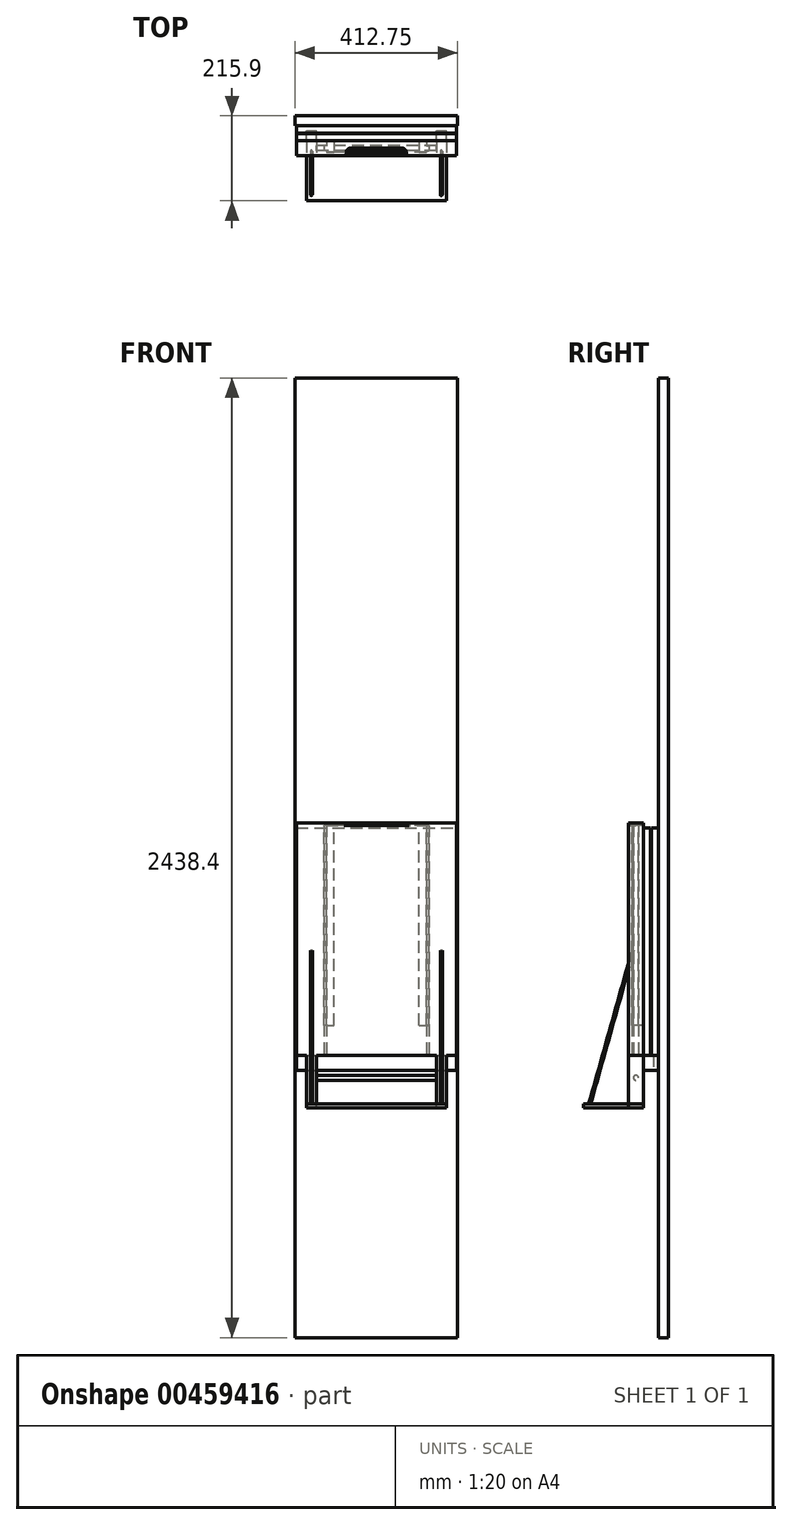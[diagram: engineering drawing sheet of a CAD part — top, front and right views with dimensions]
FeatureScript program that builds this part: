
annotation { "Feature Type Name" : "Feature", "Feature Type Description" : "" }
export const myFeature = defineFeature(function(context is Context, id is Id, definition is map)
    precondition{}
    {
        {
            var Q0;
            Q0=qCreatedBy(makeId("Front.planeOp"),FACE);
            var sketch = newSketch(context, id + "F0", { "sketchPlane" : qUnion([Q0])});
            skLineSegment(sketch, "E0.bottom", {"start": v(0, 0) * mm, "end": v(412.75, 0) * mm});
            skLineSegment(sketch, "E0.top", {"start": v(0, 2438.4) * mm, "end": v(412.75, 2438.4) * mm});
            skLineSegment(sketch, "E0.left", {"start": v(0, 0) * mm, "end": v(0, 2438.4) * mm});
            skLineSegment(sketch, "E0.right", {"start": v(412.75, 0) * mm, "end": v(412.75, 2438.4) * mm});
            skSolve(sketch);
        }
        {
            var Q0;
            Q0=qSketchRegion(id+"F0",true);
            extrude(context, id + "F1", {"entities" : qUnion([Q0]), "depth" : 25.4 * mm});
        }
        {
            var Q0;
            Q0=makeQuery(id+"F1.opExtrude","CAP_FACE",FACE,{"disambiguationData":[OSD([sQuery(id+"F0.wireOp",EDGE,"E0.bottom"),sQuery(id+"F0.wireOp",EDGE,"E0.top"),sQuery(id+"F0.wireOp",EDGE,"E0.left"),sQuery(id+"F0.wireOp",EDGE,"E0.right")])],"isStart":false});
            var sketch = newSketch(context, id + "F2", { "sketchPlane" : qUnion([Q0])});
            skLineSegment(sketch, "E1", {"start": v(206.38, 0) * mm, "end": v(206.38, 1295.4) * mm, "construction": true});
            skPoint(sketch, "E2", {"position": v(206.38, 736.6) * mm});
            skSolve(sketch);
        }
        {
            var Q0;
            Q0=makeQuery(id+"F2.imprint","IMPRINT",FACE,{"disambiguationData":[TD([[makeQuery(id+"F2.imprint","IMPRINT",EDGE,{"derivedFrom":makeQuery(id+"F1.opExtrude","CAP_EDGE",EDGE,{"disambiguationData":[OSD([sQuery(id+"F0.wireOp",EDGE,"E0.bottom")])],"isStart":false})}),1.0]])]});
            var sketch = newSketch(context, id + "F3", { "sketchPlane" : qUnion([Q0])});
            skLineSegment(sketch, "E3.bottom", {"start": v(3.17, 717.55) * mm, "end": v(409.58, 717.55) * mm});
            skLineSegment(sketch, "E3.top", {"start": v(3.18, 679.45) * mm, "end": v(409.57, 679.45) * mm});
            skLineSegment(sketch, "E3.left", {"start": v(3.17, 717.55) * mm, "end": v(3.17, 679.45) * mm});
            skLineSegment(sketch, "E3.right", {"start": v(409.57, 717.55) * mm, "end": v(409.57, 679.45) * mm});
            skLineSegment(sketch, "E4", {"start": v(206.37, 717.55) * mm, "end": v(206.37, 764.95) * mm, "construction": true});
            skSolve(sketch);
        }
        {
            var Q0;
            Q0=qSketchRegion(id+"F3",true);
            extrude(context, id + "F4", {"entities" : qUnion([Q0]), "depth" : 38.1 * mm});
        }
        {
            var Q0;
            Q0=makeQuery(id+"F4.opExtrude","SWEPT_FACE",FACE,{"disambiguationData":[OSD([sQuery(id+"F3.wireOp",EDGE,"E3.bottom")])]});
            var sketch = newSketch(context, id + "F5", { "sketchPlane" : qUnion([Q0])});
            skLineSegment(sketch, "E5.bottom", {"start": v(3.17, -25.4) * mm, "end": v(409.58, -25.4) * mm});
            skLineSegment(sketch, "E5.top", {"start": v(3.17, -43.66) * mm, "end": v(409.58, -43.66) * mm});
            skLineSegment(sketch, "E5.left", {"start": v(3.17, -25.4) * mm, "end": v(3.17, -43.66) * mm});
            skLineSegment(sketch, "E5.right", {"start": v(409.58, -25.4) * mm, "end": v(409.58, -43.66) * mm});
            skLineSegment(sketch, "E6.bottom", {"start": v(3.17, -63.5) * mm, "end": v(409.58, -63.5) * mm});
            skLineSegment(sketch, "E6.top", {"start": v(3.17, -45.24) * mm, "end": v(409.58, -45.24) * mm});
            skLineSegment(sketch, "E6.left", {"start": v(3.17, -63.5) * mm, "end": v(3.17, -45.24) * mm});
            skLineSegment(sketch, "E6.right", {"start": v(409.58, -63.5) * mm, "end": v(409.58, -45.24) * mm});
            skSolve(sketch);
        }
        {
            var Q0;
            Q0=qSketchRegion(id+"F5",true);
            var Q1;
            Q1=sQuery(id+"F2.wireOp",VERTEX,"E1.end");
            extrude(context, id + "F6", {"entities" : qUnion([Q0]), "endBound" : BoundingType.UP_TO_VERTEX, "endBoundEntityVertex" : qUnion([Q1]), "depth" : 25.4 * mm});
        }
        {
            var Q0;
            Q0=makeQuery(id+"F4.opExtrude","CAP_FACE",FACE,{"disambiguationData":[OSD([sQuery(id+"F3.wireOp",EDGE,"E3.bottom"),sQuery(id+"F3.wireOp",EDGE,"E3.top"),sQuery(id+"F3.wireOp",EDGE,"E3.left"),sQuery(id+"F3.wireOp",EDGE,"E3.right")])],"isStart":false});
            var sketch = newSketch(context, id + "F7", { "sketchPlane" : qUnion([Q0])});
            skLineSegment(sketch, "E7.bottom", {"start": v(3.17, 717.55) * mm, "end": v(28.57, 717.55) * mm});
            skLineSegment(sketch, "E7.top", {"start": v(3.17, 679.45) * mm, "end": v(28.57, 679.45) * mm});
            skLineSegment(sketch, "E7.left", {"start": v(3.17, 717.55) * mm, "end": v(3.17, 679.45) * mm});
            skLineSegment(sketch, "E7.right", {"start": v(28.57, 717.55) * mm, "end": v(28.57, 679.45) * mm});
            skLineSegment(sketch, "E8.bottom", {"start": v(409.57, 679.45) * mm, "end": v(384.17, 679.45) * mm});
            skLineSegment(sketch, "E8.top", {"start": v(409.57, 717.55) * mm, "end": v(384.17, 717.55) * mm});
            skLineSegment(sketch, "E8.left", {"start": v(409.57, 679.45) * mm, "end": v(409.57, 717.55) * mm});
            skLineSegment(sketch, "E8.right", {"start": v(384.17, 679.45) * mm, "end": v(384.17, 717.55) * mm});
            skSolve(sketch);
        }
        {
            var Q0;
            Q0=qSketchRegion(id+"F7",true);
            extrude(context, id + "F8", {"entities" : qUnion([Q0]), "depth" : 584.2 * mm});
        }
        {
            var Q0;
            Q0=makeQuery(id+"F8.opExtrude","CAP_FACE",FACE,{"disambiguationData":[OSD([sQuery(id+"F7.wireOp",EDGE,"E8.bottom"),sQuery(id+"F7.wireOp",EDGE,"E8.top"),sQuery(id+"F7.wireOp",EDGE,"E8.left"),sQuery(id+"F7.wireOp",EDGE,"E8.right")])],"isStart":false});
            var sketch = newSketch(context, id + "F9", { "sketchPlane" : qUnion([Q0])});
            skLineSegment(sketch, "E9.bottom", {"start": v(53.97, 717.55) * mm, "end": v(79.37, 717.55) * mm});
            skLineSegment(sketch, "E9.top", {"start": v(53.97, 679.45) * mm, "end": v(79.37, 679.45) * mm});
            skLineSegment(sketch, "E9.left", {"start": v(53.97, 717.55) * mm, "end": v(53.97, 679.45) * mm});
            skLineSegment(sketch, "E9.right", {"start": v(79.37, 717.55) * mm, "end": v(79.37, 704.85) * mm});
            skLineSegment(sketch, "E10.bottom", {"start": v(333.38, 717.55) * mm, "end": v(358.78, 717.55) * mm});
            skLineSegment(sketch, "E10.top", {"start": v(333.38, 679.45) * mm, "end": v(358.78, 679.45) * mm});
            skLineSegment(sketch, "E10.left", {"start": v(333.38, 717.55) * mm, "end": v(333.38, 704.85) * mm});
            skLineSegment(sketch, "E10.right", {"start": v(358.78, 717.55) * mm, "end": v(358.78, 679.45) * mm});
            skLineSegment(sketch, "E11", {"start": v(53.97, 698.5) * mm, "end": v(358.78, 698.5) * mm, "construction": true});
            skLineSegment(sketch, "E12", {"start": v(358.78, 698.5) * mm, "end": v(206.37, 698.5) * mm, "construction": true});
            skLineSegment(sketch, "E13", {"start": v(206.37, 698.5) * mm, "end": v(206.37, 1295.4) * mm, "construction": true});
            skLineSegment(sketch, "E14.bottom", {"start": v(79.37, 704.85) * mm, "end": v(73.02, 704.85) * mm});
            skLineSegment(sketch, "E14.top", {"start": v(79.37, 692.15) * mm, "end": v(73.02, 692.15) * mm});
            skLineSegment(sketch, "E14.right", {"start": v(73.02, 704.85) * mm, "end": v(73.02, 692.15) * mm});
            skLineSegment(sketch, "E15.bottom", {"start": v(333.38, 704.85) * mm, "end": v(339.73, 704.85) * mm});
            skLineSegment(sketch, "E15.top", {"start": v(333.38, 692.15) * mm, "end": v(339.73, 692.15) * mm});
            skLineSegment(sketch, "E15.right", {"start": v(339.73, 704.85) * mm, "end": v(339.73, 692.15) * mm});
            skLineSegment(sketch, "E16", {"start": v(73.02, 698.5) * mm, "end": v(91.35, 698.5) * mm, "construction": true});
            skLineSegment(sketch, "E17.trimOffspring", {"start": v(79.37, 692.15) * mm, "end": v(79.37, 679.45) * mm});
            skLineSegment(sketch, "E18.trimOffspring", {"start": v(333.38, 692.15) * mm, "end": v(333.38, 679.45) * mm});
            skSolve(sketch);
        }
        {
            var Q0;
            Q0=qSketchRegion(id+"F9",true);
            extrude(context, id + "F10", {"entities" : qUnion([Q0]), "depth" : 330.2 * mm, "hasSecondDirection" : true, "secondDirectionOppositeDirection" : true, "secondDirectionDepth" : 254 * mm});
        }
        {
            var Q0;
            Q0=makeQuery(id+"F10.opExtrude","CAP_FACE",FACE,{"disambiguationData":[OSD([sQuery(id+"F9.wireOp",EDGE,"E9.bottom"),sQuery(id+"F9.wireOp",EDGE,"E9.top"),sQuery(id+"F9.wireOp",EDGE,"E9.left"),sQuery(id+"F9.wireOp",EDGE,"E9.right"),sQuery(id+"F9.wireOp",EDGE,"E14.bottom"),sQuery(id+"F9.wireOp",EDGE,"E14.top"),sQuery(id+"F9.wireOp",EDGE,"E14.right"),sQuery(id+"F9.wireOp",EDGE,"E17.trimOffspring")])],"isStart":false});
            var sketch = newSketch(context, id + "F11", { "sketchPlane" : qUnion([Q0])});
            skLineSegment(sketch, "E19.bottom", {"start": v(53.97, 679.45) * mm, "end": v(358.78, 679.45) * mm});
            skLineSegment(sketch, "E19.top", {"start": v(53.97, 717.55) * mm, "end": v(358.78, 717.55) * mm});
            skLineSegment(sketch, "E19.left", {"start": v(53.97, 679.45) * mm, "end": v(53.97, 717.55) * mm});
            skLineSegment(sketch, "E19.right", {"start": v(358.78, 679.45) * mm, "end": v(358.78, 717.55) * mm});
            skSolve(sketch);
        }
        {
            var Q0;
            Q0=qSketchRegion(id+"F11",true);
            extrude(context, id + "F12", {"entities" : qUnion([Q0]), "depth" : 6.35 * mm});
        }
        {
            var Q0;
            Q0=makeQuery(id+"F8.opExtrude","CAP_FACE",FACE,{"disambiguationData":[OSD([sQuery(id+"F7.wireOp",EDGE,"E7.bottom"),sQuery(id+"F7.wireOp",EDGE,"E7.top"),sQuery(id+"F7.wireOp",EDGE,"E7.left"),sQuery(id+"F7.wireOp",EDGE,"E7.right")])],"isStart":false});
            var sketch = newSketch(context, id + "F13", { "sketchPlane" : qUnion([Q0])});
            skLineSegment(sketch, "E20.0", {"start": v(79.37, 717.55) * mm, "end": v(79.37, 704.85) * mm});
            skLineSegment(sketch, "E20.1", {"start": v(79.37, 704.85) * mm, "end": v(73.02, 704.85) * mm});
            skLineSegment(sketch, "E20.2", {"start": v(73.02, 704.85) * mm, "end": v(73.02, 692.15) * mm});
            skLineSegment(sketch, "E20.3", {"start": v(79.37, 692.15) * mm, "end": v(73.02, 692.15) * mm});
            skLineSegment(sketch, "E20.4", {"start": v(79.37, 692.15) * mm, "end": v(79.37, 679.45) * mm});
            skLineSegment(sketch, "E20.5", {"start": v(333.38, 717.55) * mm, "end": v(333.38, 704.85) * mm});
            skLineSegment(sketch, "E20.6", {"start": v(333.38, 704.85) * mm, "end": v(339.73, 704.85) * mm});
            skLineSegment(sketch, "E20.7", {"start": v(339.73, 704.85) * mm, "end": v(339.73, 692.15) * mm});
            skLineSegment(sketch, "E20.8", {"start": v(333.38, 692.15) * mm, "end": v(339.73, 692.15) * mm});
            skLineSegment(sketch, "E20.9", {"start": v(333.38, 692.15) * mm, "end": v(333.38, 679.45) * mm});
            skLineSegment(sketch, "E21", {"start": v(333.38, 717.55) * mm, "end": v(314.33, 717.55) * mm});
            skLineSegment(sketch, "E22", {"start": v(314.33, 717.55) * mm, "end": v(314.33, 679.45) * mm});
            skLineSegment(sketch, "E23", {"start": v(314.33, 679.45) * mm, "end": v(333.38, 679.45) * mm});
            skLineSegment(sketch, "E24", {"start": v(79.37, 717.55) * mm, "end": v(98.42, 717.55) * mm});
            skLineSegment(sketch, "E25", {"start": v(98.42, 717.55) * mm, "end": v(98.42, 679.45) * mm});
            skLineSegment(sketch, "E26", {"start": v(98.42, 679.45) * mm, "end": v(79.37, 679.45) * mm});
            skSolve(sketch);
        }
        {
            var Q0;
            Q0=qSketchRegion(id+"F13",true);
            extrude(context, id + "F14", {"entities" : qUnion([Q0]), "oppositeDirection" : true, "depth" : 508 * mm});
        }
        {
            var Q0;
            Q0=makeQuery(id+"F14.opExtrude","SWEPT_FACE",FACE,{"disambiguationData":[OSD([sQuery(id+"F13.wireOp",EDGE,"E23")])]});
            var sketch = newSketch(context, id + "F15", { "sketchPlane" : qUnion([Q0])});
            skLineSegment(sketch, "E27.bottom", {"start": v(44.15, 977.9) * mm, "end": v(373.47, 977.9) * mm});
            skLineSegment(sketch, "E27.top", {"start": v(44.15, 63.5) * mm, "end": v(373.47, 63.5) * mm});
            skLineSegment(sketch, "E27.left", {"start": v(44.15, 977.9) * mm, "end": v(44.15, 63.5) * mm});
            skLineSegment(sketch, "E27.right", {"start": v(373.47, 977.9) * mm, "end": v(373.47, 63.5) * mm});
            skSolve(sketch);
        }
        {
            var Q0;
            Q0=qSketchRegion(id+"F15",true);
            extrude(context, id + "F16", {"entities" : qUnion([Q0]), "operationType" : NewBodyOperationType.REMOVE, "oppositeDirection" : true, "depth" : 9.52 * mm});
        }
        {
            var Q0;
            Q0=makeQuery(id+"F8.opExtrude","SWEPT_FACE",FACE,{"disambiguationData":[OSD([sQuery(id+"F7.wireOp",EDGE,"E8.bottom")])]});
            var sketch = newSketch(context, id + "F17", { "sketchPlane" : qUnion([Q0])});
            skLineSegment(sketch, "E28.bottom", {"start": v(53.97, 647.7) * mm, "end": v(358.78, 647.7) * mm});
            skLineSegment(sketch, "E28.top", {"start": v(53.97, 63.5) * mm, "end": v(358.78, 63.5) * mm});
            skLineSegment(sketch, "E28.left", {"start": v(53.97, 647.7) * mm, "end": v(53.97, 63.5) * mm});
            skLineSegment(sketch, "E28.right", {"start": v(358.78, 647.7) * mm, "end": v(358.78, 63.5) * mm});
            skSolve(sketch);
        }
        {
            var Q0;
            Q0=qSketchRegion(id+"F17",true);
            var Q1;
            {var subQ5=sQuery(id+"F9.wireOp",EDGE,"E9.left");Q1=makeQuery(id+"F16.boolean.opBoolean","COPY",FACE,{"disambiguationData":[TD([makeQuery(id+"F10.opExtrude","SWEPT_FACE",FACE,{"disambiguationData":[OSD([subQ5])]})])],"derivedFrom":makeQuery(id+"F16.opExtrude","CAP_FACE",FACE,{"disambiguationData":[OSD([sQuery(id+"F15.wireOp",EDGE,"E27.bottom"),sQuery(id+"F15.wireOp",EDGE,"E27.top"),sQuery(id+"F15.wireOp",EDGE,"E27.left"),sQuery(id+"F15.wireOp",EDGE,"E27.right")])],"isStart":false})});}
            extrude(context, id + "F18", {"entities" : qUnion([Q0]), "endBound" : BoundingType.UP_TO_SURFACE, "oppositeDirection" : true, "endBoundEntityFace" : qUnion([Q1]), "depth" : 25.4 * mm});
        }
        {
            var Q0;
            Q0=makeQuery(id+"F12.opExtrude","CAP_FACE",FACE,{"disambiguationData":[OSD([sQuery(id+"F11.wireOp",EDGE,"E19.bottom"),sQuery(id+"F11.wireOp",EDGE,"E19.top"),sQuery(id+"F11.wireOp",EDGE,"E19.left"),sQuery(id+"F11.wireOp",EDGE,"E19.right")])],"isStart":false});
            var sketch = newSketch(context, id + "F19", { "sketchPlane" : qUnion([Q0])});
            skLineSegment(sketch, "E29.top", {"start": v(139.7, 698.5) * mm, "end": v(273.05, 698.5) * mm});
            skLineSegment(sketch, "E29.left", {"start": v(130.17, 685.8) * mm, "end": v(130.17, 688.98) * mm});
            skLineSegment(sketch, "E29.right", {"start": v(282.57, 685.8) * mm, "end": v(282.57, 688.98) * mm});
            skLineSegment(sketch, "E30", {"start": v(206.37, 698.5) * mm, "end": v(206.37, 717.55) * mm, "construction": true});
            skPoint(sketch, "E31.visualSharp", {"position": v(130.17, 698.5) * mm});
            skArc(sketch, "E31.filletArc", {"start": v(139.7, 698.5) * mm, "mid": v(132.96, 695.71) * mm, "end": v(130.17, 688.98) * mm});
            skPoint(sketch, "E32.visualSharp", {"position": v(282.58, 698.5) * mm});
            skArc(sketch, "E32.filletArc", {"start": v(282.57, 688.98) * mm, "mid": v(279.79, 695.71) * mm, "end": v(273.05, 698.5) * mm});
            skLineSegment(sketch, "E33", {"start": v(123.82, 679.45) * mm, "end": v(104.54, 679.45) * mm});
            skLineSegment(sketch, "E34", {"start": v(104.54, 679.45) * mm, "end": v(95.15, 663.43) * mm});
            skLineSegment(sketch, "E35", {"start": v(95.15, 663.43) * mm, "end": v(306.09, 663.43) * mm});
            skLineSegment(sketch, "E36", {"start": v(306.09, 663.43) * mm, "end": v(306.09, 679.45) * mm});
            skLineSegment(sketch, "E37", {"start": v(306.09, 679.45) * mm, "end": v(288.92, 679.45) * mm});
            skPoint(sketch, "E38.visualSharp", {"position": v(130.17, 679.45) * mm});
            skArc(sketch, "E38.filletArc", {"start": v(123.82, 679.45) * mm, "mid": v(128.32, 681.3) * mm, "end": v(130.17, 685.8) * mm});
            skPoint(sketch, "E39.visualSharp", {"position": v(282.57, 679.45) * mm});
            skArc(sketch, "E39.filletArc", {"start": v(282.58, 685.8) * mm, "mid": v(284.43, 681.3) * mm, "end": v(288.92, 679.45) * mm});
            skSolve(sketch);
        }
        {
            var Q0;
            Q0=qSketchRegion(id+"F19",true);
            extrude(context, id + "F20", {"entities" : qUnion([Q0]), "operationType" : NewBodyOperationType.REMOVE, "oppositeDirection" : true, "depth" : 25.4 * mm});
        }
        {
            var Q0;
            Q0=makeQuery(id+"F8.opExtrude","SWEPT_FACE",FACE,{"disambiguationData":[OSD([sQuery(id+"F7.wireOp",EDGE,"E7.bottom")])]});
            var sketch = newSketch(context, id + "F21", { "sketchPlane" : qUnion([Q0])});
            skLineSegment(sketch, "E40.bottom", {"start": v(3.17, -63.5) * mm, "end": v(409.58, -63.5) * mm});
            skLineSegment(sketch, "E40.top", {"start": v(3.17, -647.7) * mm, "end": v(409.58, -647.7) * mm});
            skLineSegment(sketch, "E40.left", {"start": v(3.17, -63.5) * mm, "end": v(3.17, -647.7) * mm});
            skLineSegment(sketch, "E40.right", {"start": v(409.58, -63.5) * mm, "end": v(409.58, -647.7) * mm});
            skLineSegment(sketch, "E41.bottom", {"start": v(3.17, -650.88) * mm, "end": v(409.58, -650.88) * mm});
            skLineSegment(sketch, "E41.top", {"start": v(3.17, -1235.08) * mm, "end": v(409.58, -1235.08) * mm});
            skLineSegment(sketch, "E41.left", {"start": v(3.17, -650.88) * mm, "end": v(3.17, -1235.08) * mm});
            skLineSegment(sketch, "E41.right", {"start": v(409.58, -650.88) * mm, "end": v(409.58, -1235.08) * mm});
            skSolve(sketch);
        }
        {
            var Q0;
            Q0=qSketchRegion(id+"F21",true);
            extrude(context, id + "F22", {"entities" : qUnion([Q0]), "depth" : 19.05 * mm});
        }
        {
            var Q0;
            Q0=makeQuery(id+"F22.opExtrude","CAP_FACE",FACE,{"disambiguationData":[OSD([sQuery(id+"F21.wireOp",EDGE,"E40.bottom"),sQuery(id+"F21.wireOp",EDGE,"E40.top"),sQuery(id+"F21.wireOp",EDGE,"E40.left"),sQuery(id+"F21.wireOp",EDGE,"E40.right")])],"isStart":true});
            var sketch = newSketch(context, id + "F23", { "sketchPlane" : qUnion([Q0])});
            skLineSegment(sketch, "E42.bottom", {"start": v(28.57, 635) * mm, "end": v(53.97, 635) * mm});
            skLineSegment(sketch, "E42.top", {"start": v(28.57, 596.9) * mm, "end": v(53.97, 596.9) * mm});
            skLineSegment(sketch, "E42.left", {"start": v(28.57, 635) * mm, "end": v(28.57, 596.9) * mm});
            skLineSegment(sketch, "E42.right", {"start": v(53.97, 635) * mm, "end": v(53.97, 596.9) * mm});
            skLineSegment(sketch, "E43.bottom", {"start": v(358.78, 635) * mm, "end": v(384.17, 635) * mm});
            skLineSegment(sketch, "E43.top", {"start": v(358.78, 596.9) * mm, "end": v(384.17, 596.9) * mm});
            skLineSegment(sketch, "E43.left", {"start": v(358.78, 635) * mm, "end": v(358.78, 596.9) * mm});
            skLineSegment(sketch, "E43.right", {"start": v(384.17, 635) * mm, "end": v(384.17, 596.9) * mm});
            skSolve(sketch);
        }
        {
            var Q0;
            Q0=qSketchRegion(id+"F23",true);
            var Q1;
            Q1=makeQuery(id+"F1.opExtrude","SWEPT_FACE",FACE,{"disambiguationData":[OSD([sQuery(id+"F0.wireOp",EDGE,"E0.bottom")])]});
            extrude(context, id + "F24", {"entities" : qUnion([Q0]), "endBound" : BoundingType.UP_TO_SURFACE, "endBoundEntityFace" : qUnion([Q1]), "depth" : 25.4 * mm});
        }
        {
            var Q0;
            Q0=makeQuery(id+"F24.opExtrude","CAP_FACE",FACE,{"disambiguationData":[OSD([sQuery(id+"F23.wireOp",EDGE,"E43.bottom"),sQuery(id+"F23.wireOp",EDGE,"E43.top"),sQuery(id+"F23.wireOp",EDGE,"E43.left"),sQuery(id+"F23.wireOp",EDGE,"E43.right")])],"isStart":false});
            var sketch = newSketch(context, id + "F25", { "sketchPlane" : qUnion([Q0])});
            skLineSegment(sketch, "E44.bottom", {"start": v(28.57, 596.9) * mm, "end": v(384.17, 596.9) * mm});
            skLineSegment(sketch, "E44.top", {"start": v(28.57, 749.3) * mm, "end": v(384.17, 749.3) * mm});
            skLineSegment(sketch, "E44.left", {"start": v(28.57, 596.9) * mm, "end": v(28.57, 749.3) * mm});
            skLineSegment(sketch, "E44.right", {"start": v(384.17, 596.9) * mm, "end": v(384.17, 749.3) * mm});
            skSolve(sketch);
        }
        {
            var Q0;
            Q0=qSketchRegion(id+"F25",true);
            extrude(context, id + "F26", {"entities" : qUnion([Q0]), "oppositeDirection" : true, "depth" : 9.52 * mm});
        }
        {
            var Q0;
            Q0=makeQuery(id+"F4.opExtrude","SWEPT_FACE",FACE,{"disambiguationData":[OSD([sQuery(id+"F3.wireOp",EDGE,"E3.top")])]});
            var sketch = newSketch(context, id + "F27", { "sketchPlane" : qUnion([Q0])});
            skLineSegment(sketch, "E45.bottom", {"start": v(28.57, 63.5) * mm, "end": v(53.97, 63.5) * mm});
            skLineSegment(sketch, "E45.top", {"start": v(28.57, 38.1) * mm, "end": v(53.97, 38.1) * mm});
            skLineSegment(sketch, "E45.left", {"start": v(28.57, 63.5) * mm, "end": v(28.57, 38.1) * mm});
            skLineSegment(sketch, "E45.right", {"start": v(53.97, 63.5) * mm, "end": v(53.97, 38.1) * mm});
            skLineSegment(sketch, "E46.bottom", {"start": v(358.78, 63.5) * mm, "end": v(384.18, 63.5) * mm});
            skLineSegment(sketch, "E46.top", {"start": v(358.78, 38.1) * mm, "end": v(384.18, 38.1) * mm});
            skLineSegment(sketch, "E46.left", {"start": v(358.78, 63.5) * mm, "end": v(358.78, 38.1) * mm});
            skLineSegment(sketch, "E46.right", {"start": v(384.18, 63.5) * mm, "end": v(384.18, 38.1) * mm});
            skSolve(sketch);
        }
        {
            var Q0;
            Q0=qSketchRegion(id+"F27",true);
            var Q1;
            Q1=makeQuery(id+"F4.opExtrude","SWEPT_FACE",FACE,{"disambiguationData":[OSD([sQuery(id+"F3.wireOp",EDGE,"E3.bottom")])]});
            extrude(context, id + "F28", {"entities" : qUnion([Q0]), "operationType" : NewBodyOperationType.REMOVE, "endBound" : BoundingType.UP_TO_SURFACE, "oppositeDirection" : true, "endBoundEntityFace" : qUnion([Q1]), "depth" : 25.4 * mm});
        }
        {
            var Q0;
            Q0=makeQuery(id+"F24.opExtrude","SWEPT_FACE",FACE,{"disambiguationData":[OSD([sQuery(id+"F23.wireOp",EDGE,"E42.bottom")])]});
            var sketch = newSketch(context, id + "F29", { "sketchPlane" : qUnion([Q0])});
            skLineSegment(sketch, "E47", {"start": v(28.57, 358.78) * mm, "end": v(53.97, 358.78) * mm, "construction": true});
            skLineSegment(sketch, "E48", {"start": v(41.27, 358.78) * mm, "end": v(41.27, 12.63) * mm, "construction": true});
            skLineSegment(sketch, "E49", {"start": v(358.78, 358.78) * mm, "end": v(384.17, 358.78) * mm, "construction": true});
            skLineSegment(sketch, "E50", {"start": v(371.48, 358.78) * mm, "end": v(371.48, 99.9) * mm, "construction": true});
            skSolve(sketch);
        }
        {
            var Q0;
            Q0=makeQuery(id+"F1.opExtrude","SWEPT_FACE",FACE,{"disambiguationData":[OSD([sQuery(id+"F0.wireOp",EDGE,"E0.left")])]});
            var Q1;
            Q1=sQuery(id+"F29.wireOp",EDGE,"E48");
            cPlane(context, id + "F30", {"entities" : qUnion([Q0, Q1]), "cplaneType" : CPlaneType.LINE_ANGLE, "offset" : 25.4 * mm, "angle" : 0 * degree, "width" : 152.4 * mm, "height" : 152.4 * mm});
        }
        {
            var Q0;
            Q0=sQuery(id+"F29.wireOp",EDGE,"E50");
            var Q1;
            Q1=makeQuery(id+"F1.opExtrude","SWEPT_FACE",FACE,{"disambiguationData":[OSD([sQuery(id+"F0.wireOp",EDGE,"E0.left")])]});
            cPlane(context, id + "F31", {"entities" : qUnion([Q0, Q1]), "cplaneType" : CPlaneType.LINE_ANGLE, "offset" : 25.4 * mm, "angle" : 0 * degree, "width" : 152.4 * mm, "height" : 152.4 * mm});
        }
        {
            var Q0;
            Q0=qCreatedBy(id+"F30.planeOp",FACE);
            var sketch = newSketch(context, id + "F32", { "sketchPlane" : qUnion([Q0])});
            skLineSegment(sketch, "E51", {"start": v(-635.27, 358.16) * mm, "end": v(-733.4, 9.53) * mm});
            skLineSegment(sketch, "E52", {"start": v(-635.27, 358.16) * mm, "end": v(-623.6, 399.62) * mm});
            skSolve(sketch);
        }
        {
            var Q0;
            Q0=qCreatedBy(id+"F31.planeOp",FACE);
            var sketch = newSketch(context, id + "F33", { "sketchPlane" : qUnion([Q0])});
            skLineSegment(sketch, "E53.0", {"start": v(-635.27, 358.16) * mm, "end": v(-733.4, 9.53) * mm});
            skSolve(sketch);
        }
        {
            var Q0;
            Q0=makeQuery(id+"F26.opExtrude","CAP_FACE",FACE,{"disambiguationData":[OSD([sQuery(id+"F25.wireOp",EDGE,"E44.bottom"),sQuery(id+"F25.wireOp",EDGE,"E44.top"),sQuery(id+"F25.wireOp",EDGE,"E44.left"),sQuery(id+"F25.wireOp",EDGE,"E44.right")])],"isStart":false});
            var sketch = newSketch(context, id + "F34", { "sketchPlane" : qUnion([Q0])});
            skCircle(sketch, "E54", {"center": v(41.27, -733.4) * mm, "radius": 2.54 * mm});
            skCircle(sketch, "E55", {"center": v(371.48, -733.4) * mm, "radius": 2.54 * mm});
            skSolve(sketch);
        }
        {
            var Q0;
            Q0=makeQuery(id+"F34.imprint","IMPRINT",FACE,{"disambiguationData":[TD([[makeQuery(id+"F34.imprint","IMPRINT",EDGE,{"derivedFrom":sQuery(id+"F34.wireOp",EDGE,"E54")}),1.0]])]});
            var Q1;
            Q1=makeQuery(id+"F34.imprint","IMPRINT",FACE,{"disambiguationData":[TD([[makeQuery(id+"F34.imprint","IMPRINT",EDGE,{"derivedFrom":sQuery(id+"F34.wireOp",EDGE,"E55")}),1.0]])]});
            var Q2;
            Q2=sQuery(id+"F32.wireOp",EDGE,"E51");
            var Q3;
            Q3=sQuery(id+"F32.wireOp",EDGE,"E52");
            sweep(context, id + "F35", {"profiles" : qUnion([Q0, Q1]), "path" : qUnion([Q2, Q3]), "keepProfileOrientation" : true});
        }
        {
            var Q0;
            Q0=makeQuery(id+"F24.opExtrude","SWEPT_FACE",FACE,{"disambiguationData":[OSD([sQuery(id+"F23.wireOp",EDGE,"E42.right")])]});
            var sketch = newSketch(context, id + "F36", { "sketchPlane" : qUnion([Q0])});
            skCircle(sketch, "E56", {"center": v(-615.95, 76.2) * mm, "radius": 6.35 * mm});
            skLineSegment(sketch, "E57", {"start": v(-615.95, 76.2) * mm, "end": v(-615.95, 0) * mm, "construction": true});
            skSolve(sketch);
        }
        {
            var Q0;
            Q0=qSketchRegion(id+"F36",true);
            extrude(context, id + "F37", {"entities" : qUnion([Q0]), "endBound" : BoundingType.UP_TO_NEXT, "depth" : 25.4 * mm});
        }
        {
            var Q0;
            Q0=makeQuery(id+"F22.opExtrude","SWEPT_BODY",BODY,{"disambiguationData":[OSD([sQuery(id+"F21.wireOp",EDGE,"E41.bottom"),sQuery(id+"F21.wireOp",EDGE,"E41.top"),sQuery(id+"F21.wireOp",EDGE,"E41.left"),sQuery(id+"F21.wireOp",EDGE,"E41.right")])]});
            var Q1;
            Q1=makeQuery(id+"F22.opExtrude","SWEPT_BODY",BODY,{"disambiguationData":[OSD([sQuery(id+"F21.wireOp",EDGE,"E40.bottom"),sQuery(id+"F21.wireOp",EDGE,"E40.top"),sQuery(id+"F21.wireOp",EDGE,"E40.left"),sQuery(id+"F21.wireOp",EDGE,"E40.right")])]});
            deleteBodies(context, id + "F38", {"entities" : qUnion([Q0, Q1])});
        }
        {
            var Q0;
            Q0=makeQuery(id+"F37.opExtrude","SWEPT_BODY",BODY,{"disambiguationData":[OSD([sQuery(id+"F36.wireOp",EDGE,"E56")])]});
            var Q1;
            Q1=makeQuery(id+"F35.opSweep","SWEPT_BODY",BODY,{"disambiguationData":[OSD([sQuery(id+"F32.wireOp",EDGE,"E52"),sQuery(id+"F34.wireOp",EDGE,"E55")])]});
            var Q2;
            Q2=makeQuery(id+"F35.opSweep","SWEPT_BODY",BODY,{"disambiguationData":[OSD([sQuery(id+"F32.wireOp",EDGE,"E52"),sQuery(id+"F34.wireOp",EDGE,"E54")])]});
            var Q3;
            Q3=makeQuery(id+"F26.opExtrude","SWEPT_BODY",BODY,{"disambiguationData":[OSD([sQuery(id+"F25.wireOp",EDGE,"E44.bottom"),sQuery(id+"F25.wireOp",EDGE,"E44.top"),sQuery(id+"F25.wireOp",EDGE,"E44.left"),sQuery(id+"F25.wireOp",EDGE,"E44.right")])]});
            var Q4;
            Q4=makeQuery(id+"F24.opExtrude","SWEPT_BODY",BODY,{"disambiguationData":[OSD([sQuery(id+"F23.wireOp",EDGE,"E43.bottom"),sQuery(id+"F23.wireOp",EDGE,"E43.top"),sQuery(id+"F23.wireOp",EDGE,"E43.left"),sQuery(id+"F23.wireOp",EDGE,"E43.right")])]});
            var Q5;
            Q5=makeQuery(id+"F24.opExtrude","SWEPT_BODY",BODY,{"disambiguationData":[OSD([sQuery(id+"F23.wireOp",EDGE,"E42.bottom"),sQuery(id+"F23.wireOp",EDGE,"E42.top"),sQuery(id+"F23.wireOp",EDGE,"E42.left"),sQuery(id+"F23.wireOp",EDGE,"E42.right")])]});
            var Q6;
            Q6=makeQuery(id+"F24.opExtrude","CAP_EDGE",EDGE,{"disambiguationData":[OSD([sQuery(id+"F23.wireOp",EDGE,"E43.bottom")])],"isStart":true});
            transform(context, id + "F39", {"entities" : qUnion([Q0, Q1, Q2, Q3, Q4, Q5]), "transformType" : TransformType.ROTATION, "transformAxis" : qUnion([Q6]), "angle" : 90 * degree, "makeCopy" : false});
        }
        {
            var Q0;
            Q0=makeQuery(id+"F24.opExtrude","SWEPT_BODY",BODY,{"disambiguationData":[OSD([sQuery(id+"F23.wireOp",EDGE,"E42.bottom"),sQuery(id+"F23.wireOp",EDGE,"E42.top"),sQuery(id+"F23.wireOp",EDGE,"E42.left"),sQuery(id+"F23.wireOp",EDGE,"E42.right")])]});
            var Q1;
            Q1=makeQuery(id+"F24.opExtrude","SWEPT_BODY",BODY,{"disambiguationData":[OSD([sQuery(id+"F23.wireOp",EDGE,"E43.bottom"),sQuery(id+"F23.wireOp",EDGE,"E43.top"),sQuery(id+"F23.wireOp",EDGE,"E43.left"),sQuery(id+"F23.wireOp",EDGE,"E43.right")])]});
            var Q2;
            Q2=makeQuery(id+"F26.opExtrude","SWEPT_BODY",BODY,{"disambiguationData":[OSD([sQuery(id+"F25.wireOp",EDGE,"E44.bottom"),sQuery(id+"F25.wireOp",EDGE,"E44.top"),sQuery(id+"F25.wireOp",EDGE,"E44.left"),sQuery(id+"F25.wireOp",EDGE,"E44.right")])]});
            var Q3;
            Q3=makeQuery(id+"F35.opSweep","SWEPT_BODY",BODY,{"disambiguationData":[OSD([sQuery(id+"F32.wireOp",EDGE,"E52"),sQuery(id+"F34.wireOp",EDGE,"E54")])]});
            var Q4;
            Q4=makeQuery(id+"F35.opSweep","SWEPT_BODY",BODY,{"disambiguationData":[OSD([sQuery(id+"F32.wireOp",EDGE,"E52"),sQuery(id+"F34.wireOp",EDGE,"E55")])]});
            var Q5;
            Q5=makeQuery(id+"F37.opExtrude","SWEPT_BODY",BODY,{"disambiguationData":[OSD([sQuery(id+"F36.wireOp",EDGE,"E56")])]});
            var Q6;
            Q6=makeQuery(id+"F8.opExtrude","CAP_EDGE",EDGE,{"disambiguationData":[OSD([sQuery(id+"F7.wireOp",EDGE,"E8.left")])],"isStart":false});
            transform(context, id + "F40", {"entities" : qUnion([Q0, Q1, Q2, Q3, Q4, Q5]), "transformType" : TransformType.TRANSLATION_DISTANCE, "transformDirection" : qUnion([Q6]), "distance" : 38.1 * mm, "makeCopy" : false});
        }
        {
            var Q0;
            Q0=makeQuery(id+"F24.opExtrude","SWEPT_BODY",BODY,{"disambiguationData":[OSD([sQuery(id+"F23.wireOp",EDGE,"E43.bottom"),sQuery(id+"F23.wireOp",EDGE,"E43.top"),sQuery(id+"F23.wireOp",EDGE,"E43.left"),sQuery(id+"F23.wireOp",EDGE,"E43.right")])]});
            var Q1;
            Q1=makeQuery(id+"F24.opExtrude","SWEPT_BODY",BODY,{"disambiguationData":[OSD([sQuery(id+"F23.wireOp",EDGE,"E42.bottom"),sQuery(id+"F23.wireOp",EDGE,"E42.top"),sQuery(id+"F23.wireOp",EDGE,"E42.left"),sQuery(id+"F23.wireOp",EDGE,"E42.right")])]});
            var Q2;
            Q2=makeQuery(id+"F26.opExtrude","SWEPT_BODY",BODY,{"disambiguationData":[OSD([sQuery(id+"F25.wireOp",EDGE,"E44.bottom"),sQuery(id+"F25.wireOp",EDGE,"E44.top"),sQuery(id+"F25.wireOp",EDGE,"E44.left"),sQuery(id+"F25.wireOp",EDGE,"E44.right")])]});
            var Q3;
            Q3=makeQuery(id+"F35.opSweep","SWEPT_BODY",BODY,{"disambiguationData":[OSD([sQuery(id+"F32.wireOp",EDGE,"E52"),sQuery(id+"F34.wireOp",EDGE,"E54")])]});
            var Q4;
            Q4=makeQuery(id+"F35.opSweep","SWEPT_BODY",BODY,{"disambiguationData":[OSD([sQuery(id+"F32.wireOp",EDGE,"E52"),sQuery(id+"F34.wireOp",EDGE,"E55")])]});
            var Q5;
            Q5=makeQuery(id+"F37.opExtrude","SWEPT_BODY",BODY,{"disambiguationData":[OSD([sQuery(id+"F36.wireOp",EDGE,"E56")])]});
            var Q6;
            Q6=makeQuery(id+"F8.opExtrude","SWEPT_EDGE",EDGE,{"disambiguationData":[OSD([sQuery(id+"F3.wireOp",EDGE,"E3.bottom"),sQuery(id+"F7.wireOp",EDGE,"E7.bottom"),sQuery(id+"F7.wireOp",EDGE,"E7.right")])]});
            transform(context, id + "F41", {"entities" : qUnion([Q0, Q1, Q2, Q3, Q4, Q5]), "transformType" : TransformType.TRANSLATION_DISTANCE, "transformDirection" : qUnion([Q6]), "distance" : 12.7 * mm, "oppositeDirection" : true, "makeCopy" : false});
        }
        {
            var Q0;
            Q0=makeQuery(id+"F10.opExtrude","SWEPT_BODY",BODY,{"disambiguationData":[OSD([sQuery(id+"F9.wireOp",EDGE,"E9.bottom"),sQuery(id+"F9.wireOp",EDGE,"E9.top"),sQuery(id+"F9.wireOp",EDGE,"E9.left"),sQuery(id+"F9.wireOp",EDGE,"E9.right"),sQuery(id+"F9.wireOp",EDGE,"E14.bottom"),sQuery(id+"F9.wireOp",EDGE,"E14.top"),sQuery(id+"F9.wireOp",EDGE,"E14.right"),sQuery(id+"F9.wireOp",EDGE,"E17.trimOffspring")])]});
            var Q1;
            Q1=makeQuery(id+"F12.opExtrude","SWEPT_BODY",BODY,{"disambiguationData":[OSD([sQuery(id+"F11.wireOp",EDGE,"E19.bottom"),sQuery(id+"F11.wireOp",EDGE,"E19.top"),sQuery(id+"F11.wireOp",EDGE,"E19.left"),sQuery(id+"F11.wireOp",EDGE,"E19.right")])]});
            var Q2;
            Q2=makeQuery(id+"F10.opExtrude","SWEPT_BODY",BODY,{"disambiguationData":[OSD([sQuery(id+"F9.wireOp",EDGE,"E10.bottom"),sQuery(id+"F9.wireOp",EDGE,"E10.top"),sQuery(id+"F9.wireOp",EDGE,"E10.left"),sQuery(id+"F9.wireOp",EDGE,"E10.right"),sQuery(id+"F9.wireOp",EDGE,"E15.bottom"),sQuery(id+"F9.wireOp",EDGE,"E15.top"),sQuery(id+"F9.wireOp",EDGE,"E15.right"),sQuery(id+"F9.wireOp",EDGE,"E18.trimOffspring")])]});
            var Q3;
            Q3=makeQuery(id+"F10.opExtrude","SWEPT_EDGE",EDGE,{"disambiguationData":[OSD([sQuery(id+"F9.wireOp",EDGE,"E9.bottom"),sQuery(id+"F9.wireOp",EDGE,"E9.right")])]});
            transform(context, id + "F42", {"entities" : qUnion([Q0, Q1, Q2]), "transformType" : TransformType.TRANSLATION_DISTANCE, "transformDirection" : qUnion([Q3]), "distance" : 330.2 * mm, "makeCopy" : false});
        }
        {
            var Q0;
            Q0=makeQuery(id+"F14.opExtrude","SWEPT_BODY",BODY,{"disambiguationData":[OSD([sQuery(id+"F13.wireOp",EDGE,"E20.0"),sQuery(id+"F13.wireOp",EDGE,"E20.1"),sQuery(id+"F13.wireOp",EDGE,"E20.2"),sQuery(id+"F13.wireOp",EDGE,"E20.3"),sQuery(id+"F13.wireOp",EDGE,"E20.4"),sQuery(id+"F13.wireOp",EDGE,"E24"),sQuery(id+"F13.wireOp",EDGE,"E25"),sQuery(id+"F13.wireOp",EDGE,"E26")])]});
            var Q1;
            Q1=makeQuery(id+"F14.opExtrude","SWEPT_BODY",BODY,{"disambiguationData":[OSD([sQuery(id+"F13.wireOp",EDGE,"E20.5"),sQuery(id+"F13.wireOp",EDGE,"E20.6"),sQuery(id+"F13.wireOp",EDGE,"E20.7"),sQuery(id+"F13.wireOp",EDGE,"E20.8"),sQuery(id+"F13.wireOp",EDGE,"E20.9"),sQuery(id+"F13.wireOp",EDGE,"E21"),sQuery(id+"F13.wireOp",EDGE,"E22"),sQuery(id+"F13.wireOp",EDGE,"E23")])]});
            var Q2;
            Q2=makeQuery(id+"F8.opExtrude","SWEPT_BODY",BODY,{"disambiguationData":[OSD([sQuery(id+"F7.wireOp",EDGE,"E8.bottom"),sQuery(id+"F7.wireOp",EDGE,"E8.top"),sQuery(id+"F7.wireOp",EDGE,"E8.left"),sQuery(id+"F7.wireOp",EDGE,"E8.right")])]});
            var Q3;
            Q3=makeQuery(id+"F12.opExtrude","SWEPT_BODY",BODY,{"disambiguationData":[OSD([sQuery(id+"F11.wireOp",EDGE,"E19.bottom"),sQuery(id+"F11.wireOp",EDGE,"E19.top"),sQuery(id+"F11.wireOp",EDGE,"E19.left"),sQuery(id+"F11.wireOp",EDGE,"E19.right")])]});
            var Q4;
            Q4=makeQuery(id+"F35.opSweep","SWEPT_BODY",BODY,{"disambiguationData":[OSD([sQuery(id+"F32.wireOp",EDGE,"E52"),sQuery(id+"F34.wireOp",EDGE,"E55")])]});
            var Q5;
            Q5=makeQuery(id+"F35.opSweep","SWEPT_BODY",BODY,{"disambiguationData":[OSD([sQuery(id+"F32.wireOp",EDGE,"E52"),sQuery(id+"F34.wireOp",EDGE,"E54")])]});
            var Q6;
            Q6=makeQuery(id+"F10.opExtrude","SWEPT_BODY",BODY,{"disambiguationData":[OSD([sQuery(id+"F9.wireOp",EDGE,"E10.bottom"),sQuery(id+"F9.wireOp",EDGE,"E10.top"),sQuery(id+"F9.wireOp",EDGE,"E10.left"),sQuery(id+"F9.wireOp",EDGE,"E10.right"),sQuery(id+"F9.wireOp",EDGE,"E15.bottom"),sQuery(id+"F9.wireOp",EDGE,"E15.top"),sQuery(id+"F9.wireOp",EDGE,"E15.right"),sQuery(id+"F9.wireOp",EDGE,"E18.trimOffspring")])]});
            var Q7;
            Q7=makeQuery(id+"F24.opExtrude","SWEPT_BODY",BODY,{"disambiguationData":[OSD([sQuery(id+"F23.wireOp",EDGE,"E43.bottom"),sQuery(id+"F23.wireOp",EDGE,"E43.top"),sQuery(id+"F23.wireOp",EDGE,"E43.left"),sQuery(id+"F23.wireOp",EDGE,"E43.right")])]});
            var Q8;
            Q8=makeQuery(id+"F18.opExtrude","SWEPT_BODY",BODY,{"disambiguationData":[OSD([sQuery(id+"F17.wireOp",EDGE,"E28.bottom"),sQuery(id+"F17.wireOp",EDGE,"E28.top"),sQuery(id+"F17.wireOp",EDGE,"E28.left"),sQuery(id+"F17.wireOp",EDGE,"E28.right")])]});
            var Q9;
            Q9=makeQuery(id+"F8.opExtrude","SWEPT_BODY",BODY,{"disambiguationData":[OSD([sQuery(id+"F7.wireOp",EDGE,"E7.bottom"),sQuery(id+"F7.wireOp",EDGE,"E7.top"),sQuery(id+"F7.wireOp",EDGE,"E7.left"),sQuery(id+"F7.wireOp",EDGE,"E7.right")])]});
            var Q10;
            Q10=makeQuery(id+"F10.opExtrude","SWEPT_BODY",BODY,{"disambiguationData":[OSD([sQuery(id+"F9.wireOp",EDGE,"E9.bottom"),sQuery(id+"F9.wireOp",EDGE,"E9.top"),sQuery(id+"F9.wireOp",EDGE,"E9.left"),sQuery(id+"F9.wireOp",EDGE,"E9.right"),sQuery(id+"F9.wireOp",EDGE,"E14.bottom"),sQuery(id+"F9.wireOp",EDGE,"E14.top"),sQuery(id+"F9.wireOp",EDGE,"E14.right"),sQuery(id+"F9.wireOp",EDGE,"E17.trimOffspring")])]});
            var Q11;
            Q11=makeQuery(id+"F24.opExtrude","SWEPT_BODY",BODY,{"disambiguationData":[OSD([sQuery(id+"F23.wireOp",EDGE,"E42.bottom"),sQuery(id+"F23.wireOp",EDGE,"E42.top"),sQuery(id+"F23.wireOp",EDGE,"E42.left"),sQuery(id+"F23.wireOp",EDGE,"E42.right")])]});
            var Q12;
            Q12=makeQuery(id+"F26.opExtrude","SWEPT_BODY",BODY,{"disambiguationData":[OSD([sQuery(id+"F25.wireOp",EDGE,"E44.bottom"),sQuery(id+"F25.wireOp",EDGE,"E44.top"),sQuery(id+"F25.wireOp",EDGE,"E44.left"),sQuery(id+"F25.wireOp",EDGE,"E44.right")])]});
            var Q13;
            Q13=makeQuery(id+"F37.opExtrude","SWEPT_BODY",BODY,{"disambiguationData":[OSD([sQuery(id+"F36.wireOp",EDGE,"E56")])]});
            var Q14;
            {var subQ0=sQuery(id+"F3.wireOp",EDGE,"E3.bottom");Q14=makeQuery(id+"F28.boolean.opBoolean","SPLIT",EDGE,{"disambiguationData":[TD([makeQuery(id+"F28.opExtrude","SWEPT_FACE",FACE,{"disambiguationData":[OSD([sQuery(id+"F27.wireOp",EDGE,"E45.right")])]})])],"derivedFrom":makeQuery(id+"F4.opExtrude","CAP_EDGE",EDGE,{"disambiguationData":[OSD([subQ0])],"isStart":false})});}
            transform(context, id + "F43", {"entities" : qUnion([Q0, Q1, Q2, Q3, Q4, Q5, Q6, Q7, Q8, Q9, Q10, Q11, Q12, Q13]), "transformType" : TransformType.ROTATION, "transformAxis" : qUnion([Q14]), "angle" : 90 * degree, "oppositeDirection" : true, "makeCopy" : false});
        }
        {
            var Q0;
            Q0=makeQuery(id+"F12.opExtrude","CAP_FACE",FACE,{"disambiguationData":[OSD([sQuery(id+"F11.wireOp",EDGE,"E19.bottom"),sQuery(id+"F11.wireOp",EDGE,"E19.top"),sQuery(id+"F11.wireOp",EDGE,"E19.left"),sQuery(id+"F11.wireOp",EDGE,"E19.right")])],"isStart":false});
            var sketch = newSketch(context, id + "F44", { "sketchPlane" : qUnion([Q0])});
            skLineSegment(sketch, "E58.bottom", {"start": v(358.78, -63.5) * mm, "end": v(409.58, -63.5) * mm});
            skLineSegment(sketch, "E58.top", {"start": v(358.78, -101.6) * mm, "end": v(409.58, -101.6) * mm});
            skLineSegment(sketch, "E58.left", {"start": v(358.78, -63.5) * mm, "end": v(358.78, -101.6) * mm});
            skLineSegment(sketch, "E58.right", {"start": v(409.58, -63.5) * mm, "end": v(409.58, -101.6) * mm});
            skLineSegment(sketch, "E59.bottom", {"start": v(53.97, -101.6) * mm, "end": v(3.17, -101.6) * mm});
            skLineSegment(sketch, "E59.top", {"start": v(53.97, -63.5) * mm, "end": v(3.17, -63.5) * mm});
            skLineSegment(sketch, "E59.left", {"start": v(53.97, -101.6) * mm, "end": v(53.97, -63.5) * mm});
            skLineSegment(sketch, "E59.right", {"start": v(3.17, -101.6) * mm, "end": v(3.17, -63.5) * mm});
            skSolve(sketch);
        }
        {
            var Q0;
            Q0 = qSketchRegion(id + "F44", true);
            extrude(context, id + "F45", {"entities" : qUnion([Q0]), "operationType" : NewBodyOperationType.ADD, "oppositeDirection" : true, "depth" : 6.35 * mm});
        }
    });
